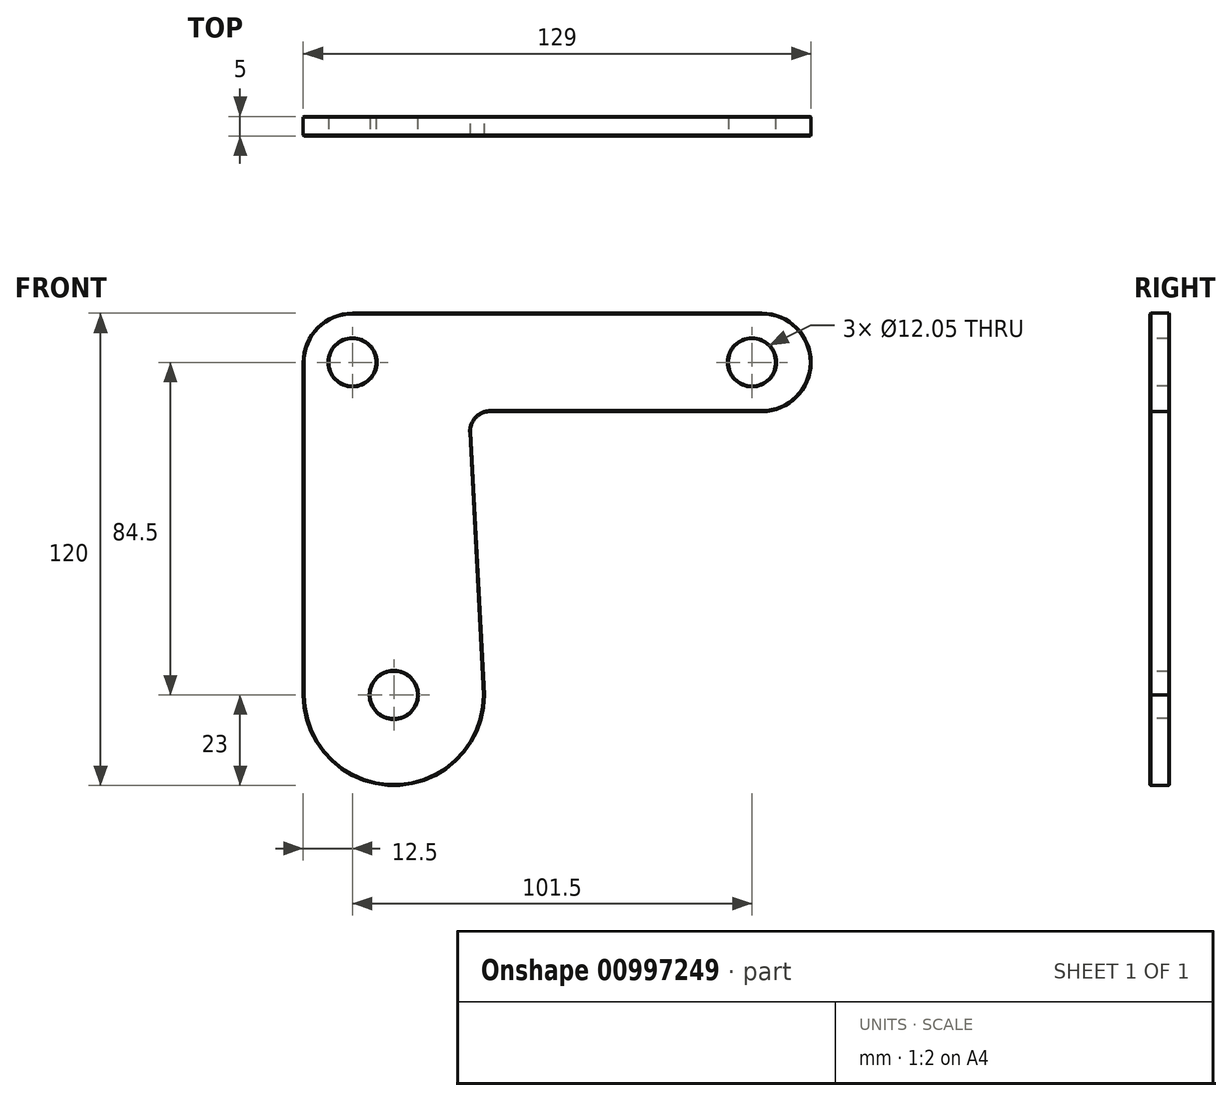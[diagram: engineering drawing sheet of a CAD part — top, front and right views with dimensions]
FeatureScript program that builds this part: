
annotation { "Feature Type Name" : "Feature", "Feature Type Description" : "" }
export const myFeature = defineFeature(function(context is Context, id is Id, definition is map)
    precondition{}
    {
        {
            var Q0;
            Q0=qCreatedBy(makeId("Front.planeOp"),FACE);
            var sketch = newSketch(context, id + "F0", { "sketchPlane" : qUnion([Q0])});
            skLineSegment(sketch, "E0", {"start": v(-64.5, -37) * mm, "end": v(-64.5, 47.5) * mm});
            skLineSegment(sketch, "E1", {"start": v(-52, 60) * mm, "end": v(52, 60) * mm});
            skLineSegment(sketch, "E2", {"start": v(52, 35) * mm, "end": v(-17, 35) * mm});
            skArc(sketch, "E3", {"start": v(-17, 35) * mm, "mid": v(-20.63, 33.44) * mm, "end": v(-22, 29.74) * mm});
            skArc(sketch, "E4", {"start": v(52, 35) * mm, "mid": v(64.5, 47.5) * mm, "end": v(52, 60) * mm});
            skArc(sketch, "E5", {"start": v(-64.5, -37) * mm, "mid": v(-41.5, -60) * mm, "end": v(-18.5, -37) * mm});
            skLineSegment(sketch, "E6", {"start": v(-18.5, -37) * mm, "end": v(-22, 29.74) * mm});
            skArc(sketch, "E7", {"start": v(-52, 60) * mm, "mid": v(-60.84, 56.34) * mm, "end": v(-64.5, 47.5) * mm});
            skLineSegment(sketch, "E8", {"start": v(0, 104.18) * mm, "end": v(0, -107.57) * mm, "construction": true});
            skLineSegment(sketch, "E9", {"start": v(-95.08, 0) * mm, "end": v(92.22, 0) * mm, "construction": true});
            skSolve(sketch);
        }
        {
            var Q0;
            Q0 = qSketchRegion(id + "F0", true);
            extrude(context, id + "F1", {"entities" : qUnion([Q0]), "endBound" : BoundingType.SYMMETRIC, "depth" : 5 * mm, "offsetDistance" : 25 * mm});
        }
        {
            var Q0;
            Q0=qCreatedBy(makeId("Front.planeOp"),FACE);
            var sketch = newSketch(context, id + "F2", { "sketchPlane" : qUnion([Q0])});
            skCircle(sketch, "E10", {"center": v(-41.5, -37) * mm, "radius": 6.03 * mm});
            skCircle(sketch, "E11", {"center": v(-52, 47.5) * mm, "radius": 6.03 * mm});
            skCircle(sketch, "E12", {"center": v(49.5, 47.5) * mm, "radius": 6.03 * mm});
            skSolve(sketch);
        }
        {
            var Q0;
            Q0 = qSketchRegion(id + "F2", true);
            extrude(context, id + "F3", {"entities" : qUnion([Q0]), "operationType" : NewBodyOperationType.REMOVE, "oppositeDirection" : true, "depth" : 25 * mm, "offsetDistance" : 25 * mm, "hasSecondDirection" : true, "secondDirectionOppositeDirection" : false, "secondDirectionDepth" : 25 * mm});
        }
        {
            var Q0;
            Q0=makeQuery(id+"F1.opExtrude","CAP_FACE",FACE,{"disambiguationData":[OSD([sQuery(id+"F0.wireOp",EDGE,"E0"),sQuery(id+"F0.wireOp",EDGE,"E1"),sQuery(id+"F0.wireOp",EDGE,"E2"),sQuery(id+"F0.wireOp",EDGE,"E3"),sQuery(id+"F0.wireOp",EDGE,"E4"),sQuery(id+"F0.wireOp",EDGE,"E5"),sQuery(id+"F0.wireOp",EDGE,"E6"),sQuery(id+"F0.wireOp",EDGE,"E7")])],"isStart":false});
            var Q1;
            Q1=makeQuery(id+"F1.opExtrude","CAP_FACE",FACE,{"disambiguationData":[OSD([sQuery(id+"F0.wireOp",EDGE,"E0"),sQuery(id+"F0.wireOp",EDGE,"E1"),sQuery(id+"F0.wireOp",EDGE,"E2"),sQuery(id+"F0.wireOp",EDGE,"E3"),sQuery(id+"F0.wireOp",EDGE,"E4"),sQuery(id+"F0.wireOp",EDGE,"E5"),sQuery(id+"F0.wireOp",EDGE,"E6"),sQuery(id+"F0.wireOp",EDGE,"E7")])],"isStart":true});
            chamfer(context, id + "F4", {"entities" : qUnion([Q0, Q1]), "width" : 0.2 * mm, "tangentPropagation" : true});
        }
    });
